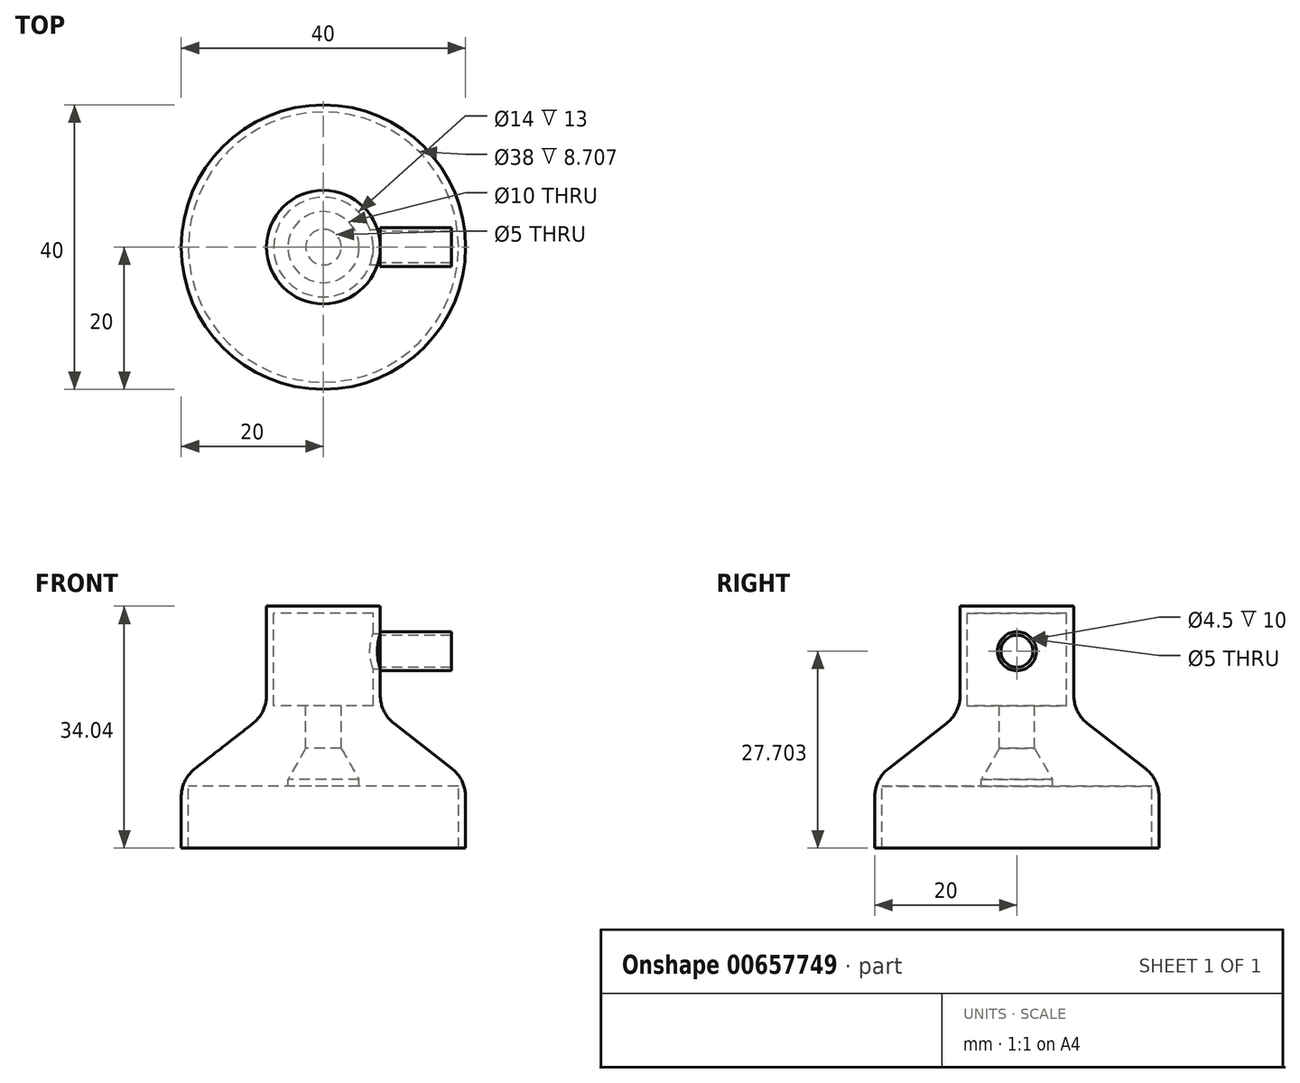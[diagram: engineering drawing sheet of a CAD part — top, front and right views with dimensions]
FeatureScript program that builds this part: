
annotation { "Feature Type Name" : "Feature", "Feature Type Description" : "" }
export const myFeature = defineFeature(function(context is Context, id is Id, definition is map)
    precondition{}
    {
        {
            var Q0;
            Q0=qCreatedBy(makeId("Front.planeOp"),FACE);
            var sketch = newSketch(context, id + "F0", { "sketchPlane" : qUnion([Q0])});
            skLineSegment(sketch, "E0.bottom", {"start": v(-20, 4.7) * mm, "end": v(-6.15, 4.7) * mm});
            skLineSegment(sketch, "E1.0", {"start": v(-19, 3.7) * mm, "end": v(-5, 3.7) * mm});
            skLineSegment(sketch, "E2.0", {"start": v(-19, 3.7) * mm, "end": v(-19, -5) * mm});
            skLineSegment(sketch, "E3", {"start": v(-5, 4.7) * mm, "end": v(-2.5, 9.04) * mm});
            skLineSegment(sketch, "E4", {"start": v(-5, 4.7) * mm, "end": v(-5, 3.7) * mm});
            skLineSegment(sketch, "E5.0", {"start": v(-6.15, 4.7) * mm, "end": v(-3.08, 10.04) * mm});
            skLineSegment(sketch, "E6.left", {"start": v(-3.08, 10.04) * mm, "end": v(-3.08, 14.03) * mm});
            skLineSegment(sketch, "E7.left", {"start": v(-2.5, 10.04) * mm, "end": v(-2.5, 13.44) * mm});
            skLineSegment(sketch, "E8", {"start": v(-2.5, 9.04) * mm, "end": v(-2.5, 10.04) * mm});
            skPoint(sketch, "E9.orphan", {"position": v(-6.73, 3.7) * mm});
            skLineSegment(sketch, "E10.bottom", {"start": v(-8, 29.04) * mm, "end": v(0, 29.04) * mm});
            skLineSegment(sketch, "E10.top", {"start": v(-8, 14.04) * mm, "end": v(-3.08, 14.04) * mm});
            skLineSegment(sketch, "E10.left", {"start": v(-8, 29.04) * mm, "end": v(-8, 14.04) * mm});
            skLineSegment(sketch, "E11", {"start": v(-8, 14.04) * mm, "end": v(-20, 4.7) * mm});
            skLineSegment(sketch, "E12.0", {"start": v(-7, 28.04) * mm, "end": v(0, 28.04) * mm});
            skLineSegment(sketch, "E13.0", {"start": v(-7, 28.04) * mm, "end": v(-7, 15.04) * mm});
            skLineSegment(sketch, "E14.0", {"start": v(-7, 15.04) * mm, "end": v(-2.5, 15.04) * mm});
            skLineSegment(sketch, "E15", {"start": v(-3.08, 14.03) * mm, "end": v(-3.08, 14.04) * mm});
            skLineSegment(sketch, "E16", {"start": v(-2.5, 13.44) * mm, "end": v(-2.5, 15.04) * mm});
            skPoint(sketch, "E17.orphan", {"position": v(-3.08, 15.04) * mm});
            skLineSegment(sketch, "E18.MirrorCS", {"start": v(-20, 4.7) * mm, "end": v(-20, -5) * mm});
            skLineSegment(sketch, "E19.MirrorCS", {"start": v(-19, -5) * mm, "end": v(-20, -5) * mm});
            skLineSegment(sketch, "E20", {"start": v(0, 29.04) * mm, "end": v(0, 28.04) * mm});
            skSolve(sketch);
        }
        {
            var Q0;
            Q0 = qSketchRegion(id + "F0", true);
            var Q1;
            Q1=sQuery(id+"F0.wireOp",EDGE,"E20");
            revolve(context, id + "F1", {"entities" : qUnion([Q0]), "axis" : qUnion([Q1]), "revolveType" : RevolveType.FULL});
        }
        {
            var Q0;
            Q0=makeQuery(id+"F1.opRevolve","SWEPT_EDGE",EDGE,{"disambiguationData":[OSD([sQuery(id+"F0.wireOp",EDGE,"E10.top"),sQuery(id+"F0.wireOp",EDGE,"E10.left"),sQuery(id+"F0.wireOp",EDGE,"E11")])]});
            fillet(context, id + "F2", {"entities" : qUnion([Q0]), "radius" : 5 * mm, "tangentPropagation" : true, "allowEdgeOverflow" : false});
        }
        {
            var Q0;
            Q0=qCreatedBy(makeId("Right.planeOp"),FACE);
            cPlane(context, id + "F3", {"entities" : qUnion([Q0]), "cplaneType" : CPlaneType.OFFSET, "offset" : 8 * mm, "width" : 150 * mm, "height" : 150 * mm});
        }
        {
            var Q0;
            Q0=qCreatedBy(id+"F3.planeOp",FACE);
            var sketch = newSketch(context, id + "F4", { "sketchPlane" : qUnion([Q0])});
            skCircle(sketch, "E21", {"center": v(0, 22.7) * mm, "radius": 2.25 * mm});
            skCircle(sketch, "E22", {"center": v(0, 22.7) * mm, "radius": 2.74 * mm});
            skSolve(sketch);
        }
        {
            var Q0;
            Q0=sQuery(id+"F4.wireOp",VERTEX,"E21.center");
            var Q1;
            Q1=makeQuery(id+"F1.opRevolve","SWEPT_BODY",BODY,{"disambiguationData":[OSD([sQuery(id+"F0.wireOp",EDGE,"E1.0"),sQuery(id+"F0.wireOp",EDGE,"E2.0"),sQuery(id+"F0.wireOp",EDGE,"E3"),sQuery(id+"F0.wireOp",EDGE,"E4"),sQuery(id+"F0.wireOp",EDGE,"E7.left"),sQuery(id+"F0.wireOp",EDGE,"E8"),sQuery(id+"F0.wireOp",EDGE,"E10.bottom"),sQuery(id+"F0.wireOp",EDGE,"E10.left"),sQuery(id+"F0.wireOp",EDGE,"E11"),sQuery(id+"F0.wireOp",EDGE,"E12.0"),sQuery(id+"F0.wireOp",EDGE,"E13.0"),sQuery(id+"F0.wireOp",EDGE,"E14.0"),sQuery(id+"F0.wireOp",EDGE,"E16"),sQuery(id+"F0.wireOp",EDGE,"E18.MirrorCS"),sQuery(id+"F0.wireOp",EDGE,"E19.MirrorCS"),sQuery(id+"F0.wireOp",EDGE,"E20")])]});
            hole(context, id + "F5", {"style" : HoleStyle.SIMPLE, "endStyle" : HoleEndStyle.BLIND, "holeDiameter" : 5 * mm, "majorDiameter" : 5 * mm, "holeDepth" : 12 * mm, "isTappedThrough" : true, "tappedDepth" : 12 * mm, "tapClearance" : 3, "startFromSketch" : true, "locations" : qUnion([Q0]), "scope" : qUnion([Q1])});
        }
        {
            var Q0;
            Q0 = qSketchRegion(id + "F4", true);
            extrude(context, id + "F6", {"entities" : qUnion([Q0]), "depth" : 10 * mm, "offsetDistance" : 25 * mm});
        }
        {
            var Q0;
            Q0=makeQuery(id+"F1.opRevolve","SWEPT_EDGE",EDGE,{"disambiguationData":[OSD([sQuery(id+"F0.wireOp",EDGE,"E0.bottom"),sQuery(id+"F0.wireOp",EDGE,"E11"),sQuery(id+"F0.wireOp",EDGE,"E18.MirrorCS")])]});
            fillet(context, id + "F7", {"entities" : qUnion([Q0]), "radius" : 5 * mm, "tangentPropagation" : true, "allowEdgeOverflow" : false});
        }
    });
